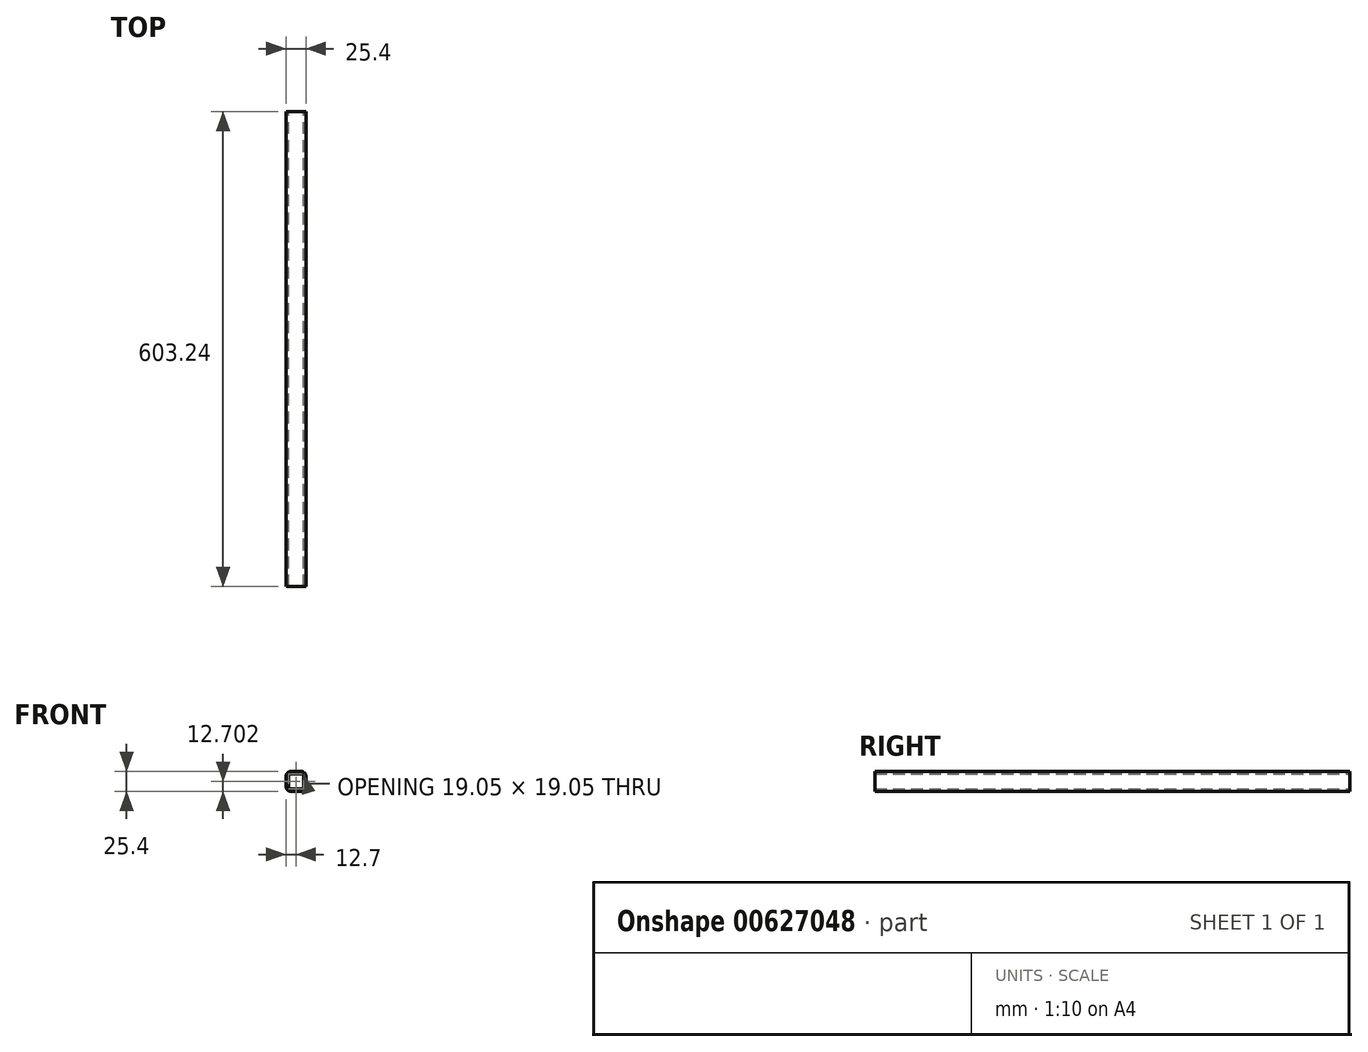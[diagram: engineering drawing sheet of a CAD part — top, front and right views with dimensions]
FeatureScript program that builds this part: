
annotation { "Feature Type Name" : "Feature", "Feature Type Description" : "" }
export const myFeature = defineFeature(function(context is Context, id is Id, definition is map)
    precondition{}
    {
        {
            var Q0;
            Q0=qCreatedBy(makeId("Front.planeOp"),FACE);
            var sketch = newSketch(context, id + "F0", { "sketchPlane" : qUnion([Q0])});
            skLineSegment(sketch, "E0.bottom", {"start": v(-6.35, 13.31) * mm, "end": v(6.35, 13.31) * mm});
            skLineSegment(sketch, "E0.top", {"start": v(-6.35, -12.09) * mm, "end": v(6.35, -12.09) * mm});
            skLineSegment(sketch, "E0.left", {"start": v(-12.7, 6.96) * mm, "end": v(-12.7, -5.74) * mm});
            skLineSegment(sketch, "E0.right", {"start": v(12.7, 6.96) * mm, "end": v(12.7, -5.74) * mm});
            skPoint(sketch, "E0.middle", {"position": v(0, 0.61) * mm});
            skPoint(sketch, "E1.visualSharp", {"position": v(-12.7, 13.31) * mm});
            skArc(sketch, "E1.filletArc", {"start": v(-11.77, 10.28) * mm, "mid": v(-12.46, 8.68) * mm, "end": v(-12.7, 6.96) * mm});
            skPoint(sketch, "E2.visualSharp", {"position": v(-6.35, 13.31) * mm});
            skArc(sketch, "E2.filletArc", {"start": v(-6.35, 13.31) * mm, "mid": v(-9.45, 12.5) * mm, "end": v(-11.77, 10.28) * mm});
            skPoint(sketch, "E3.visualSharp", {"position": v(12.7, 13.31) * mm});
            skArc(sketch, "E3.filletArc", {"start": v(12.7, 6.96) * mm, "mid": v(10.84, 11.45) * mm, "end": v(6.35, 13.31) * mm});
            skPoint(sketch, "E4.visualSharp", {"position": v(12.7, -12.09) * mm});
            skArc(sketch, "E4.filletArc", {"start": v(6.35, -12.09) * mm, "mid": v(10.84, -10.23) * mm, "end": v(12.7, -5.74) * mm});
            skPoint(sketch, "E5.visualSharp", {"position": v(-12.7, -12.09) * mm});
            skArc(sketch, "E5.filletArc", {"start": v(-12.7, -5.74) * mm, "mid": v(-10.84, -10.23) * mm, "end": v(-6.35, -12.09) * mm});
            skLineSegment(sketch, "E6.0", {"start": v(-9.52, 6.96) * mm, "end": v(-9.53, -5.74) * mm});
            skArc(sketch, "E6.1", {"start": v(-9.53, -5.74) * mm, "mid": v(-8.6, -7.98) * mm, "end": v(-6.35, -8.91) * mm});
            skLineSegment(sketch, "E6.2", {"start": v(-6.35, -8.91) * mm, "end": v(6.35, -8.91) * mm});
            skArc(sketch, "E6.3", {"start": v(6.35, -8.91) * mm, "mid": v(8.6, -7.98) * mm, "end": v(9.52, -5.74) * mm});
            skArc(sketch, "E6.4", {"start": v(-6.35, 10.14) * mm, "mid": v(-8.6, 9.2) * mm, "end": v(-9.52, 6.96) * mm});
            skLineSegment(sketch, "E6.5", {"start": v(-6.35, 10.14) * mm, "end": v(6.35, 10.14) * mm});
            skArc(sketch, "E6.6", {"start": v(9.53, 6.96) * mm, "mid": v(8.6, 9.2) * mm, "end": v(6.35, 10.14) * mm});
            skLineSegment(sketch, "E6.7", {"start": v(9.53, 6.96) * mm, "end": v(9.52, -5.74) * mm});
            skSolve(sketch);
        }
        {
            var Q0;
            Q0=qSketchRegion(id+"F0",true);
            extrude(context, id + "F1", {"entities" : qUnion([Q0]), "endBound" : BoundingType.SYMMETRIC, "depth" : 603.25 * mm, "offsetDistance" : 25.4 * mm});
        }
    });
